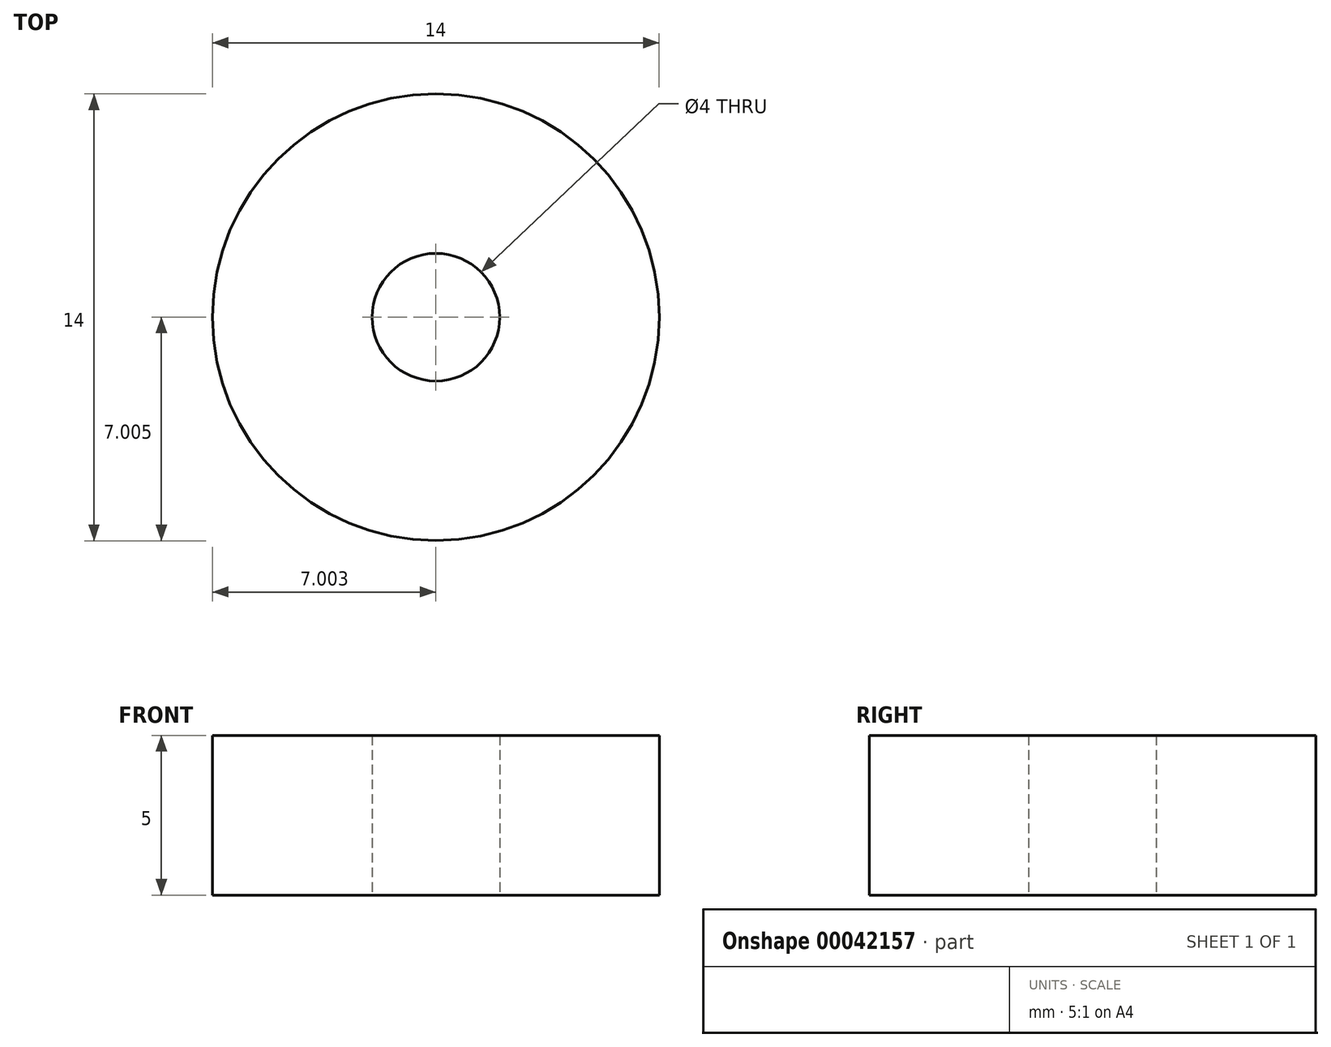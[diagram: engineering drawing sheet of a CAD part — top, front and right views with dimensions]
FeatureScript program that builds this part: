
annotation { "Feature Type Name" : "Feature", "Feature Type Description" : "" }
export const myFeature = defineFeature(function(context is Context, id is Id, definition is map)
    precondition{}
    {
        {
            var Q0;
            Q0=qCreatedBy(makeId("Top.planeOp"),FACE);
            var sketch = newSketch(context, id + "F0", { "sketchPlane" : qUnion([Q0])});
            skCircle(sketch, "E0", {"center": v(-55.23, 21.7) * mm, "radius": 2 * mm});
            skCircle(sketch, "E1", {"center": v(-55.23, 21.7) * mm, "radius": 7 * mm});
            skSolve(sketch);
        }
        {
            var Q0;
            Q0=makeQuery(id+"F0.imprint","IMPRINT",FACE,{"disambiguationData":[TD([[makeQuery(id+"F0.imprint","IMPRINT",EDGE,{"derivedFrom":sQuery(id+"F0.wireOp",EDGE,"E0")}),-1.0]])]});
            extrude(context, id + "F1", {"entities" : qUnion([Q0]), "depth" : 5 * mm});
        }
    });
